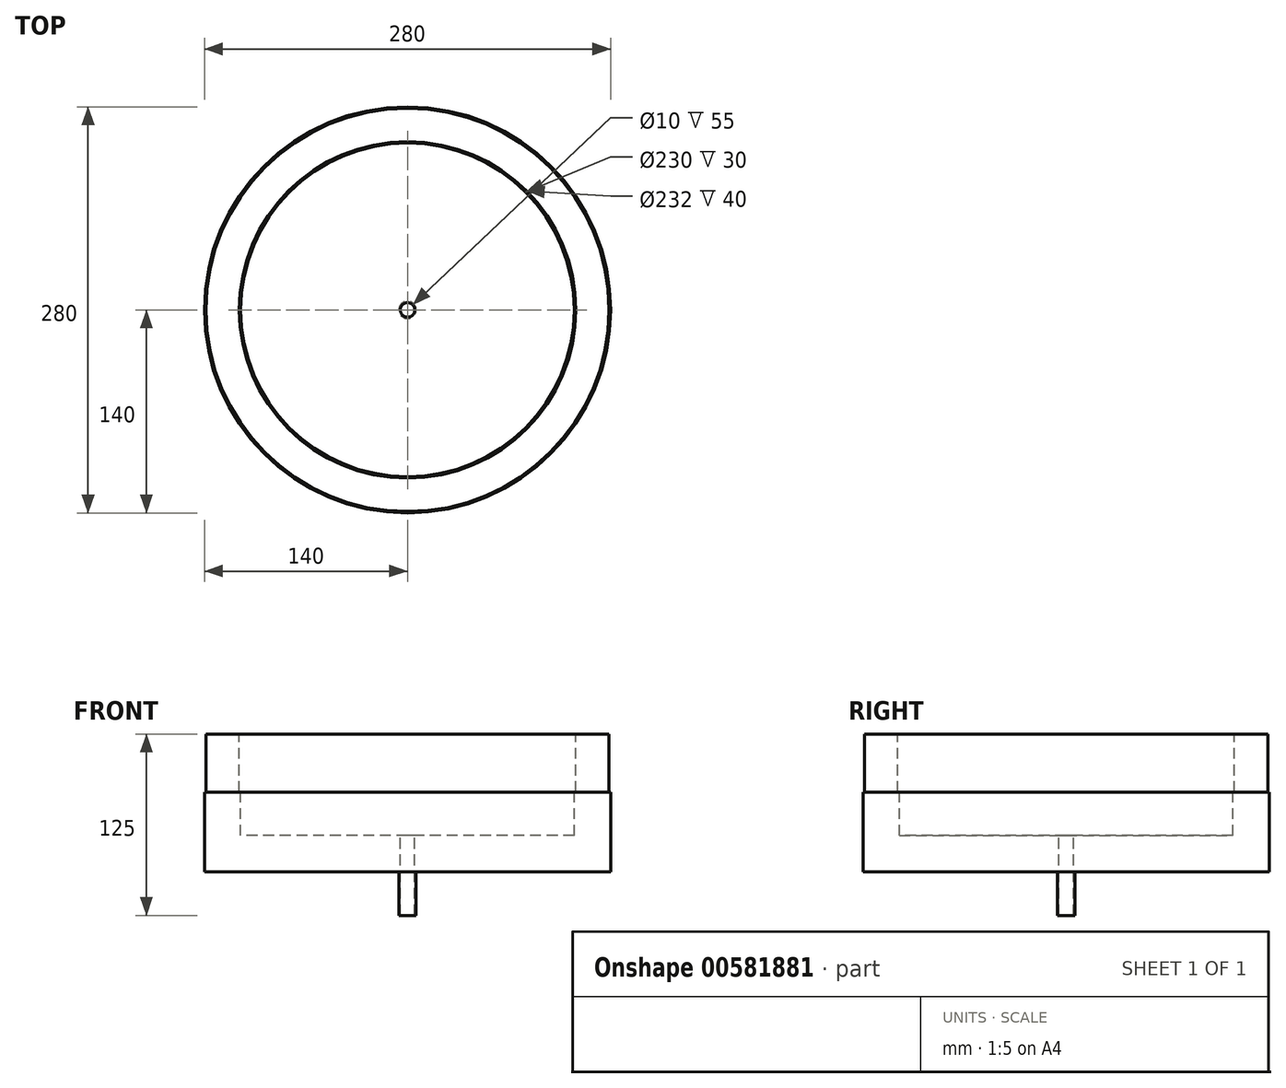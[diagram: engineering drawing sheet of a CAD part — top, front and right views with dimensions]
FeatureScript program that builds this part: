
annotation { "Feature Type Name" : "Feature", "Feature Type Description" : "" }
export const myFeature = defineFeature(function(context is Context, id is Id, definition is map)
    precondition{}
    {
        {
            var Q0;
            Q0=qCreatedBy(makeId("Front.planeOp"),FACE);
            var sketch = newSketch(context, id + "F0", { "sketchPlane" : qUnion([Q0])});
            skLineSegment(sketch, "E0", {"start": v(0, 136.7) * mm, "end": v(0, 25) * mm, "construction": true});
            skLineSegment(sketch, "E1", {"start": v(-6, 0) * mm, "end": v(-140, 0) * mm});
            skLineSegment(sketch, "E2", {"start": v(-140, 0) * mm, "end": v(-140, 55) * mm});
            skLineSegment(sketch, "E3", {"start": v(-140, 55) * mm, "end": v(-139, 55) * mm});
            skLineSegment(sketch, "E4", {"start": v(-139, 55) * mm, "end": v(-139, 95) * mm});
            skLineSegment(sketch, "E5", {"start": v(-139, 95) * mm, "end": v(-116, 95) * mm});
            skLineSegment(sketch, "E6", {"start": v(-116, 95) * mm, "end": v(-116, 55) * mm});
            skLineSegment(sketch, "E7", {"start": v(-116, 55) * mm, "end": v(-115, 55) * mm});
            skLineSegment(sketch, "E8", {"start": v(-115, 55) * mm, "end": v(-115, 25) * mm});
            skLineSegment(sketch, "E9", {"start": v(-115, 25) * mm, "end": v(-5, 25) * mm});
            skLineSegment(sketch, "E10.bottom", {"start": v(-5, 25) * mm, "end": v(-6, 25) * mm});
            skLineSegment(sketch, "E10.top", {"start": v(-5, -30) * mm, "end": v(-6, -30) * mm});
            skLineSegment(sketch, "E10.left", {"start": v(-5, 25) * mm, "end": v(-5, -30) * mm});
            skLineSegment(sketch, "E10.right", {"start": v(-6, 0) * mm, "end": v(-6, -30) * mm});
            skPoint(sketch, "E11.end.orphan", {"position": v(0, 0) * mm});
            skSolve(sketch);
        }
        {
            var Q0;
            Q0=qSketchRegion(id+"F0",true);
            var Q1;
            Q1=sQuery(id+"F0.wireOp",EDGE,"E0");
            revolve(context, id + "F1", {"surfaceOperationType" : NewSurfaceOperationType.NEW, "entities" : qUnion([Q0]), "axis" : qUnion([Q1]), "revolveType" : RevolveType.FULL});
        }
    });
